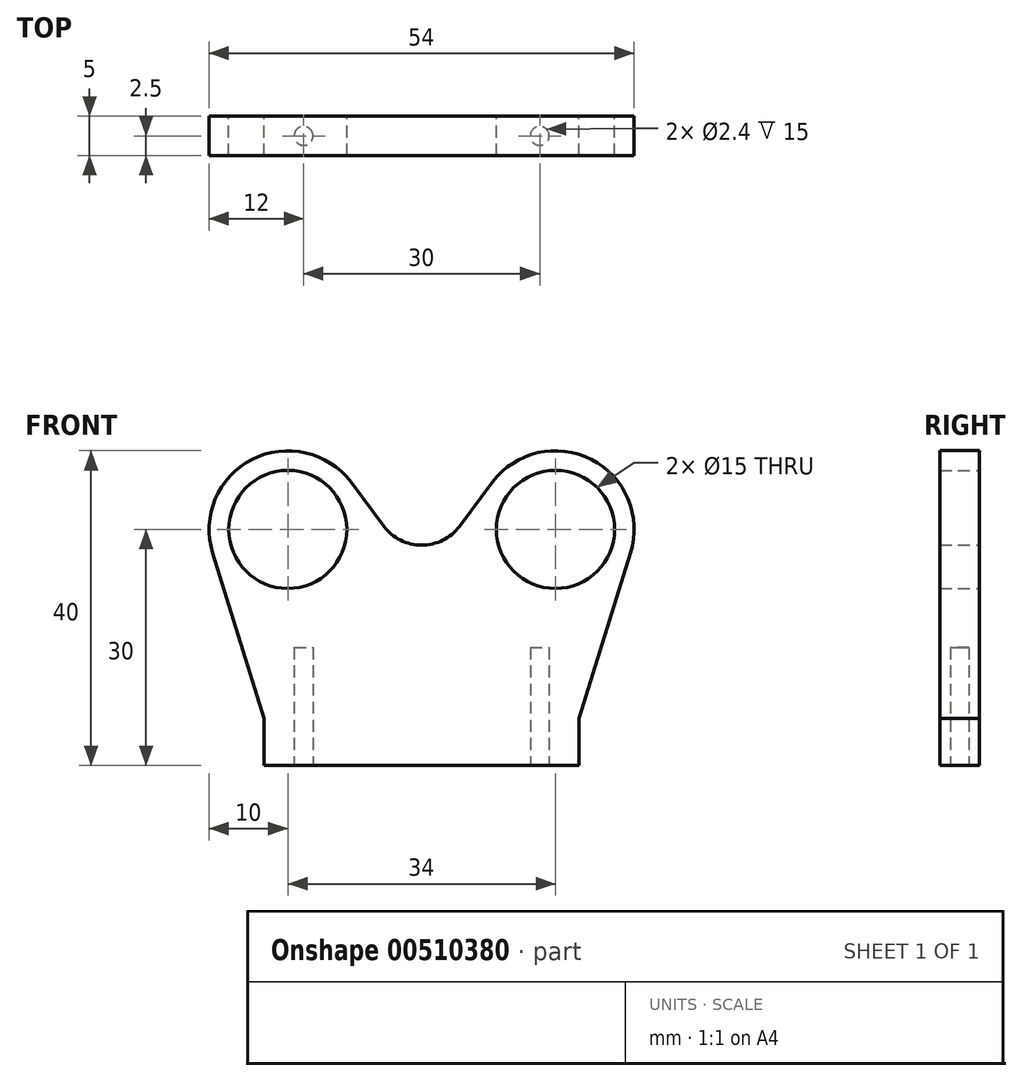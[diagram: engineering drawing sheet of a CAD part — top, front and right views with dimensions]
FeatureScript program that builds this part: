
annotation { "Feature Type Name" : "Feature", "Feature Type Description" : "" }
export const myFeature = defineFeature(function(context is Context, id is Id, definition is map)
    precondition{}
    {
        {
            var Q0;
            Q0=qCreatedBy(makeId("Front.planeOp"),FACE);
            var sketch = newSketch(context, id + "F0", { "sketchPlane" : qUnion([Q0])});
            skCircle(sketch, "E0", {"center": v(-17, 30) * mm, "radius": 7.5 * mm});
            skArc(sketch, "E1", {"start": v(-9, 36) * mm, "mid": v(-21.55, 38.9) * mm, "end": v(-26.55, 27.03) * mm});
            skArc(sketch, "E2", {"start": v(-4.8, 30.4) * mm, "mid": v(-2.68, 28.63) * mm, "end": v(0, 28) * mm});
            skLineSegment(sketch, "E3", {"start": v(-9, 36) * mm, "end": v(-4.8, 30.4) * mm});
            skLineSegment(sketch, "E4", {"start": v(0, 0) * mm, "end": v(0, 44.8) * mm, "construction": true});
            skLineSegment(sketch, "E5", {"start": v(-20, 6) * mm, "end": v(-20, 0) * mm});
            skLineSegment(sketch, "E6", {"start": v(-20, 0) * mm, "end": v(0, 0) * mm});
            skLineSegment(sketch, "E7", {"start": v(-20, 6) * mm, "end": v(-26.55, 27.03) * mm});
            skArc(sketch, "E8.MirrorCS", {"start": v(9, 36) * mm, "mid": v(21.55, 38.9) * mm, "end": v(26.55, 27.03) * mm});
            skLineSegment(sketch, "E9.MirrorCS", {"start": v(20, 6) * mm, "end": v(26.55, 27.03) * mm});
            skArc(sketch, "E10.MirrorCS", {"start": v(4.8, 30.4) * mm, "mid": v(2.68, 28.63) * mm, "end": v(0, 28) * mm});
            skCircle(sketch, "E11.MirrorC", {"center": v(17, 30) * mm, "radius": 7.5 * mm});
            skLineSegment(sketch, "E12.MirrorCS", {"start": v(20, 6) * mm, "end": v(20, 0) * mm});
            skLineSegment(sketch, "E13.MirrorCS", {"start": v(9, 36) * mm, "end": v(4.8, 30.4) * mm});
            skLineSegment(sketch, "E14.MirrorCS", {"start": v(20, 0) * mm, "end": v(0, 0) * mm});
            skSolve(sketch);
        }
        {
            var Q0;
            Q0 = qSketchRegion(id + "F0", true);
            extrude(context, id + "F1", {"entities" : qUnion([Q0]), "depth" : 2.5 * mm, "hasSecondDirection" : true, "secondDirectionOppositeDirection" : true, "secondDirectionDepth" : 2.5 * mm});
        }
        {
            var Q0;
            Q0=makeQuery(id+"F1.opExtrude","SWEPT_FACE",FACE,{"disambiguationData":[OSD([sQuery(id+"F0.wireOp",EDGE,"E6"),sQuery(id+"F0.wireOp",EDGE,"E14.MirrorCS")])]});
            var sketch = newSketch(context, id + "F2", { "sketchPlane" : qUnion([Q0])});
            skCircle(sketch, "E15", {"center": v(-15, 0) * mm, "radius": 1.2 * mm});
            skCircle(sketch, "E16", {"center": v(15, 0) * mm, "radius": 1.2 * mm});
            skSolve(sketch);
        }
        {
            var Q0;
            Q0 = qSketchRegion(id + "F2", true);
            extrude(context, id + "F3", {"entities" : qUnion([Q0]), "operationType" : NewBodyOperationType.REMOVE, "oppositeDirection" : true, "depth" : 15 * mm});
        }
    });
